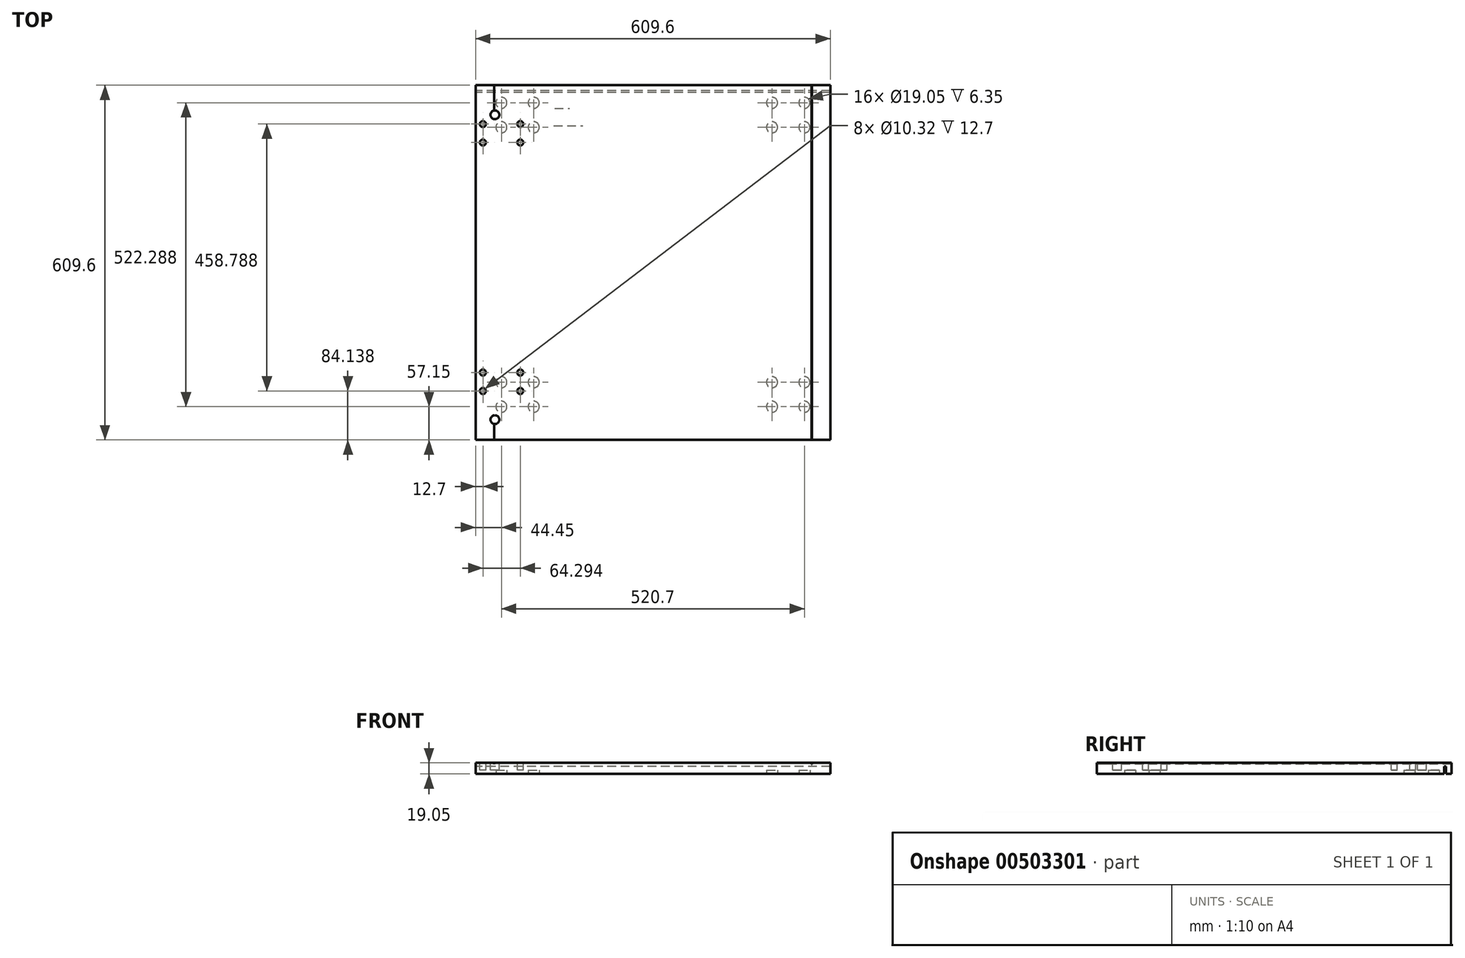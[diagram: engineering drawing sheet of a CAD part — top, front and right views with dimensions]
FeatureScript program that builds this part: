
annotation { "Feature Type Name" : "Feature", "Feature Type Description" : "" }
export const myFeature = defineFeature(function(context is Context, id is Id, definition is map)
    precondition{}
    {
        {
            var Q0;
            Q0=qCreatedBy(makeId("Top.planeOp"),FACE);
            var sketch = newSketch(context, id + "F0", { "sketchPlane" : qUnion([Q0])});
            skLineSegment(sketch, "E0.bottom", {"start": v(-304.8, 304.8) * mm, "end": v(304.8, 304.8) * mm});
            skLineSegment(sketch, "E0.top", {"start": v(-304.8, -304.8) * mm, "end": v(304.8, -304.8) * mm});
            skLineSegment(sketch, "E0.left", {"start": v(-304.8, 304.8) * mm, "end": v(-304.8, -304.8) * mm});
            skLineSegment(sketch, "E0.right", {"start": v(304.8, 304.8) * mm, "end": v(304.8, -304.8) * mm});
            skLineSegment(sketch, "E1", {"start": v(393.38, -304.8) * mm, "end": v(393.38, -188.91) * mm, "construction": true});
            skLineSegment(sketch, "E2", {"start": v(393.38, -188.91) * mm, "end": v(-304.8, -188.91) * mm, "construction": true});
            skLineSegment(sketch, "E3", {"start": v(344.85, -304.8) * mm, "end": v(344.85, -220.66) * mm, "construction": true});
            skLineSegment(sketch, "E4", {"start": v(344.85, -220.66) * mm, "end": v(-304.8, -220.66) * mm, "construction": true});
            skLineSegment(sketch, "E5", {"start": v(321.2, -304.8) * mm, "end": v(321.2, -269.88) * mm, "construction": true});
            skLineSegment(sketch, "E6", {"start": v(321.2, -269.88) * mm, "end": v(-304.8, -269.88) * mm, "construction": true});
            skLineSegment(sketch, "E7", {"start": v(-304.8, 419.45) * mm, "end": v(-227.8, 419.45) * mm, "construction": true});
            skLineSegment(sketch, "E8", {"start": v(-227.8, 419.45) * mm, "end": v(-227.8, -220.66) * mm, "construction": true});
            skPoint(sketch, "E9", {"position": v(-227.8, -188.91) * mm});
            skLineSegment(sketch, "E10", {"start": v(-304.8, 379.03) * mm, "end": v(-292.1, 379.03) * mm, "construction": true});
            skLineSegment(sketch, "E11", {"start": v(-292.1, 379.03) * mm, "end": v(-292.1, -220.66) * mm, "construction": true});
            skPoint(sketch, "E12", {"position": v(-292.1, -188.91) * mm});
            skLineSegment(sketch, "E13", {"start": v(-304.8, 399.62) * mm, "end": v(-271.46, 399.62) * mm, "construction": true});
            skLineSegment(sketch, "E14", {"start": v(-271.46, 399.62) * mm, "end": v(-271.46, -269.88) * mm, "construction": true});
            skCircle(sketch, "E15", {"center": v(-271.46, -269.88) * mm, "radius": 7.54 * mm});
            skCircle(sketch, "E16", {"center": v(-227.8, -220.66) * mm, "radius": 5.16 * mm});
            skCircle(sketch, "E17", {"center": v(-227.8, -188.91) * mm, "radius": 5.16 * mm});
            skCircle(sketch, "E18", {"center": v(-292.1, -188.91) * mm, "radius": 5.16 * mm});
            skCircle(sketch, "E19", {"center": v(-292.1, -220.66) * mm, "radius": 5.16 * mm});
            skLineSegment(sketch, "E20", {"start": v(396.02, 304.8) * mm, "end": v(396.02, 206.37) * mm, "construction": true});
            skLineSegment(sketch, "E21", {"start": v(319.7, 304.8) * mm, "end": v(319.7, 254) * mm, "construction": true});
            skLineSegment(sketch, "E22", {"start": v(353.84, 304.8) * mm, "end": v(353.84, 238.12) * mm, "construction": true});
            skLineSegment(sketch, "E23", {"start": v(319.7, 254) * mm, "end": v(-304.8, 254) * mm, "construction": true});
            skLineSegment(sketch, "E24", {"start": v(353.84, 238.12) * mm, "end": v(-304.8, 238.12) * mm, "construction": true});
            skLineSegment(sketch, "E25", {"start": v(396.02, 206.37) * mm, "end": v(-304.8, 206.38) * mm, "construction": true});
            skPoint(sketch, "E26", {"position": v(-271.46, 254) * mm});
            skPoint(sketch, "E27", {"position": v(-292.1, 238.12) * mm});
            skPoint(sketch, "E28", {"position": v(-292.1, 206.38) * mm});
            skPoint(sketch, "E29", {"position": v(-227.8, 206.38) * mm});
            skPoint(sketch, "E30", {"position": v(-227.8, 238.12) * mm});
            skCircle(sketch, "E31", {"center": v(-271.46, 254) * mm, "radius": 7.54 * mm});
            skCircle(sketch, "E32", {"center": v(-227.8, 238.12) * mm, "radius": 5.16 * mm});
            skCircle(sketch, "E33", {"center": v(-292.1, 238.12) * mm, "radius": 5.16 * mm});
            skCircle(sketch, "E34", {"center": v(-292.1, 206.38) * mm, "radius": 5.16 * mm});
            skCircle(sketch, "E35", {"center": v(-227.8, 206.38) * mm, "radius": 5.16 * mm});
            skPoint(sketch, "E36", {"position": v(0, 304.8) * mm});
            skPoint(sketch, "E37", {"position": v(304.8, 0) * mm});
            skSolve(sketch);
        }
        {
            var Q0;
            Q0=makeQuery(id+"F0.imprint","IMPRINT",FACE,{"disambiguationData":[TD([[makeQuery(id+"F0.imprint","IMPRINT",EDGE,{"derivedFrom":sQuery(id+"F0.wireOp",EDGE,"E0.bottom")}),-1.0]])]});
            var Q1;
            Q1=makeQuery(id+"F0.imprint","IMPRINT",FACE,{"disambiguationData":[TD([[makeQuery(id+"F0.imprint","IMPRINT",EDGE,{"derivedFrom":sQuery(id+"F0.wireOp",EDGE,"E31")}),1.0]])]});
            var Q2;
            Q2=makeQuery(id+"F0.imprint","IMPRINT",FACE,{"disambiguationData":[TD([[makeQuery(id+"F0.imprint","IMPRINT",EDGE,{"derivedFrom":sQuery(id+"F0.wireOp",EDGE,"E33")}),1.0]])]});
            var Q3;
            Q3=makeQuery(id+"F0.imprint","IMPRINT",FACE,{"disambiguationData":[TD([[makeQuery(id+"F0.imprint","IMPRINT",EDGE,{"derivedFrom":sQuery(id+"F0.wireOp",EDGE,"E34")}),1.0]])]});
            var Q4;
            Q4=makeQuery(id+"F0.imprint","IMPRINT",FACE,{"disambiguationData":[TD([[makeQuery(id+"F0.imprint","IMPRINT",EDGE,{"derivedFrom":sQuery(id+"F0.wireOp",EDGE,"E35")}),1.0]])]});
            var Q5;
            Q5=makeQuery(id+"F0.imprint","IMPRINT",FACE,{"disambiguationData":[TD([[makeQuery(id+"F0.imprint","IMPRINT",EDGE,{"derivedFrom":sQuery(id+"F0.wireOp",EDGE,"E32")}),1.0]])]});
            var Q6;
            Q6=makeQuery(id+"F0.imprint","IMPRINT",FACE,{"disambiguationData":[TD([[makeQuery(id+"F0.imprint","IMPRINT",EDGE,{"derivedFrom":sQuery(id+"F0.wireOp",EDGE,"E17")}),1.0]])]});
            var Q7;
            Q7=makeQuery(id+"F0.imprint","IMPRINT",FACE,{"disambiguationData":[TD([[makeQuery(id+"F0.imprint","IMPRINT",EDGE,{"derivedFrom":sQuery(id+"F0.wireOp",EDGE,"E16")}),1.0]])]});
            var Q8;
            Q8=makeQuery(id+"F0.imprint","IMPRINT",FACE,{"disambiguationData":[TD([[makeQuery(id+"F0.imprint","IMPRINT",EDGE,{"derivedFrom":sQuery(id+"F0.wireOp",EDGE,"E19")}),1.0]])]});
            var Q9;
            Q9=makeQuery(id+"F0.imprint","IMPRINT",FACE,{"disambiguationData":[TD([[makeQuery(id+"F0.imprint","IMPRINT",EDGE,{"derivedFrom":sQuery(id+"F0.wireOp",EDGE,"E18")}),1.0]])]});
            var Q10;
            Q10=makeQuery(id+"F0.imprint","IMPRINT",FACE,{"disambiguationData":[TD([[makeQuery(id+"F0.imprint","IMPRINT",EDGE,{"derivedFrom":sQuery(id+"F0.wireOp",EDGE,"E15")}),1.0]])]});
            extrude(context, id + "F1", {"entities" : qUnion([Q0, Q1, Q2, Q3, Q4, Q5, Q6, Q7, Q8, Q9, Q10]), "oppositeDirection" : true, "depth" : 19.05 * mm});
        }
        {
            var Q0;
            Q0=makeQuery(id+"F0.imprint","IMPRINT",FACE,{"disambiguationData":[TD([[makeQuery(id+"F0.imprint","IMPRINT",EDGE,{"derivedFrom":sQuery(id+"F0.wireOp",EDGE,"E15")}),1.0]])]});
            var Q1;
            Q1=makeQuery(id+"F0.imprint","IMPRINT",FACE,{"disambiguationData":[TD([[makeQuery(id+"F0.imprint","IMPRINT",EDGE,{"derivedFrom":sQuery(id+"F0.wireOp",EDGE,"E19")}),1.0]])]});
            var Q2;
            Q2=makeQuery(id+"F0.imprint","IMPRINT",FACE,{"disambiguationData":[TD([[makeQuery(id+"F0.imprint","IMPRINT",EDGE,{"derivedFrom":sQuery(id+"F0.wireOp",EDGE,"E16")}),1.0]])]});
            var Q3;
            Q3=makeQuery(id+"F0.imprint","IMPRINT",FACE,{"disambiguationData":[TD([[makeQuery(id+"F0.imprint","IMPRINT",EDGE,{"derivedFrom":sQuery(id+"F0.wireOp",EDGE,"E17")}),1.0]])]});
            var Q4;
            Q4=makeQuery(id+"F0.imprint","IMPRINT",FACE,{"disambiguationData":[TD([[makeQuery(id+"F0.imprint","IMPRINT",EDGE,{"derivedFrom":sQuery(id+"F0.wireOp",EDGE,"E18")}),1.0]])]});
            var Q5;
            Q5=makeQuery(id+"F0.imprint","IMPRINT",FACE,{"disambiguationData":[TD([[makeQuery(id+"F0.imprint","IMPRINT",EDGE,{"derivedFrom":sQuery(id+"F0.wireOp",EDGE,"E34")}),1.0]])]});
            var Q6;
            Q6=makeQuery(id+"F0.imprint","IMPRINT",FACE,{"disambiguationData":[TD([[makeQuery(id+"F0.imprint","IMPRINT",EDGE,{"derivedFrom":sQuery(id+"F0.wireOp",EDGE,"E35")}),1.0]])]});
            var Q7;
            Q7=makeQuery(id+"F0.imprint","IMPRINT",FACE,{"disambiguationData":[TD([[makeQuery(id+"F0.imprint","IMPRINT",EDGE,{"derivedFrom":sQuery(id+"F0.wireOp",EDGE,"E32")}),1.0]])]});
            var Q8;
            Q8=makeQuery(id+"F0.imprint","IMPRINT",FACE,{"disambiguationData":[TD([[makeQuery(id+"F0.imprint","IMPRINT",EDGE,{"derivedFrom":sQuery(id+"F0.wireOp",EDGE,"E33")}),1.0]])]});
            var Q9;
            Q9=makeQuery(id+"F0.imprint","IMPRINT",FACE,{"disambiguationData":[TD([[makeQuery(id+"F0.imprint","IMPRINT",EDGE,{"derivedFrom":sQuery(id+"F0.wireOp",EDGE,"E31")}),1.0]])]});
            extrude(context, id + "F2", {"entities" : qUnion([Q0, Q1, Q2, Q3, Q4, Q5, Q6, Q7, Q8, Q9]), "operationType" : NewBodyOperationType.REMOVE, "oppositeDirection" : true, "depth" : 12.7 * mm});
        }
        {
            var Q0;
            Q0=makeQuery(id+"F1.opExtrude","CAP_FACE",FACE,{"disambiguationData":[OSD([sQuery(id+"F0.wireOp",EDGE,"E0.bottom"),sQuery(id+"F0.wireOp",EDGE,"E0.top"),sQuery(id+"F0.wireOp",EDGE,"E0.left"),sQuery(id+"F0.wireOp",EDGE,"E0.right")])],"isStart":false});
            var sketch = newSketch(context, id + "F3", { "sketchPlane" : qUnion([Q0])});
            skLineSegment(sketch, "E38", {"start": v(176.5, -304.8) * mm, "end": v(176.5, -295.28) * mm, "construction": true});
            skLineSegment(sketch, "E39.bottom", {"start": v(304.8, -295.28) * mm, "end": v(-304.8, -295.28) * mm});
            skLineSegment(sketch, "E39.top", {"start": v(304.8, -292.1) * mm, "end": v(-304.8, -292.1) * mm});
            skLineSegment(sketch, "E39.left", {"start": v(304.8, -295.28) * mm, "end": v(304.8, -292.1) * mm});
            skLineSegment(sketch, "E39.right", {"start": v(-304.8, -295.28) * mm, "end": v(-304.8, -292.1) * mm});
            skSolve(sketch);
        }
        {
            var Q0;
            Q0=makeQuery(id+"F3.imprint","IMPRINT",FACE,{"disambiguationData":[TD([[makeQuery(id+"F3.imprint","IMPRINT",EDGE,{"derivedFrom":sQuery(id+"F3.wireOp",EDGE,"E39.bottom")}),-1.0]])]});
            extrude(context, id + "F4", {"entities" : qUnion([Q0]), "operationType" : NewBodyOperationType.REMOVE, "oppositeDirection" : true, "depth" : 12.7 * mm});
        }
        {
            var Q0;
            {var subQ0=sQuery(id+"F0.wireOp",EDGE,"E0.top");var subQ1=sQuery(id+"F0.wireOp",EDGE,"E0.left");var subQ2=sQuery(id+"F0.wireOp",EDGE,"E0.right");Q0=makeQuery(id+"F4.boolean.opBoolean","SPLIT",FACE,{"disambiguationData":[TD([makeQuery(id+"F1.opExtrude","SWEPT_FACE",FACE,{"disambiguationData":[OSD([subQ0])]})])],"derivedFrom":makeQuery(id+"F1.opExtrude","CAP_FACE",FACE,{"disambiguationData":[OSD([sQuery(id+"F0.wireOp",EDGE,"E0.bottom"),subQ0,subQ1,subQ2])],"isStart":false})});}
            var sketch = newSketch(context, id + "F5", { "sketchPlane" : qUnion([Q0])});
            skLineSegment(sketch, "E40", {"start": v(304.8, -324.97) * mm, "end": v(260.35, -324.97) * mm, "construction": true});
            skLineSegment(sketch, "E41", {"start": v(260.35, 304.8) * mm, "end": v(260.35, -324.35) * mm, "construction": true});
            skLineSegment(sketch, "E42", {"start": v(-304.8, -347.9) * mm, "end": v(-260.35, -347.9) * mm, "construction": true});
            skLineSegment(sketch, "E43", {"start": v(-260.35, 304.8) * mm, "end": v(-260.35, -347.28) * mm, "construction": true});
            skLineSegment(sketch, "E44", {"start": v(260.35, -324.35) * mm, "end": v(204.79, -324.35) * mm, "construction": true});
            skLineSegment(sketch, "E45", {"start": v(204.79, -324.35) * mm, "end": v(204.79, 304.8) * mm, "construction": true});
            skLineSegment(sketch, "E46", {"start": v(-260.35, -347.9) * mm, "end": v(-204.79, -347.9) * mm, "construction": true});
            skLineSegment(sketch, "E47", {"start": v(-204.79, -347.9) * mm, "end": v(-204.79, 304.8) * mm, "construction": true});
            skLineSegment(sketch, "E48", {"start": v(0, 304.8) * mm, "end": v(0, 247.65) * mm, "construction": true});
            skPoint(sketch, "E48.endSnap0", {"position": v(0, 304.8) * mm});
            skLineSegment(sketch, "E49", {"start": v(260.35, 247.65) * mm, "end": v(-260.35, 247.65) * mm, "construction": true});
            skLineSegment(sketch, "E50.0", {"start": v(-304.8, -304.8) * mm, "end": v(304.8, -304.8) * mm});
            skLineSegment(sketch, "E51", {"start": v(0, -304.8) * mm, "end": v(0, -274.64) * mm, "construction": true});
            skPoint(sketch, "E51.endSnap0", {"position": v(0, -292.1) * mm});
            skLineSegment(sketch, "E52", {"start": v(260.35, -274.64) * mm, "end": v(-260.35, -274.64) * mm, "construction": true});
            skLineSegment(sketch, "E53", {"start": v(0, 247.65) * mm, "end": v(0, 205.58) * mm, "construction": true});
            skLineSegment(sketch, "E54", {"start": v(0, -274.64) * mm, "end": v(0, -232.57) * mm, "construction": true});
            skLineSegment(sketch, "E55", {"start": v(260.35, -232.57) * mm, "end": v(-260.35, -232.57) * mm, "construction": true});
            skLineSegment(sketch, "E56", {"start": v(260.35, 205.58) * mm, "end": v(-260.35, 205.58) * mm, "construction": true});
            skCircle(sketch, "E57", {"center": v(260.35, 205.58) * mm, "radius": 9.53 * mm});
            skCircle(sketch, "E58", {"center": v(204.79, 205.58) * mm, "radius": 9.53 * mm});
            skCircle(sketch, "E59", {"center": v(204.79, 247.65) * mm, "radius": 9.53 * mm});
            skCircle(sketch, "E60", {"center": v(-204.79, 205.58) * mm, "radius": 9.53 * mm});
            skCircle(sketch, "E61", {"center": v(260.35, 247.65) * mm, "radius": 9.53 * mm});
            skCircle(sketch, "E62", {"center": v(-260.35, 205.58) * mm, "radius": 9.53 * mm});
            skCircle(sketch, "E63", {"center": v(260.35, -232.57) * mm, "radius": 9.53 * mm});
            skCircle(sketch, "E64", {"center": v(204.79, -232.57) * mm, "radius": 9.53 * mm});
            skCircle(sketch, "E65", {"center": v(204.79, -274.64) * mm, "radius": 9.53 * mm});
            skCircle(sketch, "E66", {"center": v(260.35, -274.64) * mm, "radius": 9.53 * mm});
            skCircle(sketch, "E67", {"center": v(-204.79, -274.64) * mm, "radius": 9.53 * mm});
            skCircle(sketch, "E68", {"center": v(-260.35, -274.64) * mm, "radius": 9.53 * mm});
            skCircle(sketch, "E69", {"center": v(-260.35, -232.57) * mm, "radius": 9.53 * mm});
            skCircle(sketch, "E70", {"center": v(-204.79, -232.57) * mm, "radius": 9.53 * mm});
            skCircle(sketch, "E71", {"center": v(-260.35, 247.65) * mm, "radius": 9.53 * mm});
            skCircle(sketch, "E72", {"center": v(-204.79, 247.65) * mm, "radius": 9.53 * mm});
            skSolve(sketch);
        }
        {
            var Q0;
            Q0=makeQuery(id+"F5.imprint","IMPRINT",FACE,{"disambiguationData":[TD([[makeQuery(id+"F5.imprint","IMPRINT",EDGE,{"derivedFrom":sQuery(id+"F5.wireOp",EDGE,"E66")}),1.0]])]});
            var Q1;
            Q1=makeQuery(id+"F5.imprint","IMPRINT",FACE,{"disambiguationData":[TD([[makeQuery(id+"F5.imprint","IMPRINT",EDGE,{"derivedFrom":sQuery(id+"F5.wireOp",EDGE,"E65")}),1.0]])]});
            var Q2;
            Q2=makeQuery(id+"F5.imprint","IMPRINT",FACE,{"disambiguationData":[TD([[makeQuery(id+"F5.imprint","IMPRINT",EDGE,{"derivedFrom":sQuery(id+"F5.wireOp",EDGE,"E64")}),1.0]])]});
            var Q3;
            Q3=makeQuery(id+"F5.imprint","IMPRINT",FACE,{"disambiguationData":[TD([[makeQuery(id+"F5.imprint","IMPRINT",EDGE,{"derivedFrom":sQuery(id+"F5.wireOp",EDGE,"E63")}),1.0]])]});
            var Q4;
            Q4=makeQuery(id+"F5.imprint","IMPRINT",FACE,{"disambiguationData":[TD([[makeQuery(id+"F5.imprint","IMPRINT",EDGE,{"derivedFrom":sQuery(id+"F5.wireOp",EDGE,"E67")}),1.0]])]});
            var Q5;
            Q5=makeQuery(id+"F5.imprint","IMPRINT",FACE,{"disambiguationData":[TD([[makeQuery(id+"F5.imprint","IMPRINT",EDGE,{"derivedFrom":sQuery(id+"F5.wireOp",EDGE,"E68")}),1.0]])]});
            var Q6;
            Q6=makeQuery(id+"F5.imprint","IMPRINT",FACE,{"disambiguationData":[TD([[makeQuery(id+"F5.imprint","IMPRINT",EDGE,{"derivedFrom":sQuery(id+"F5.wireOp",EDGE,"E69")}),1.0]])]});
            var Q7;
            Q7=makeQuery(id+"F5.imprint","IMPRINT",FACE,{"disambiguationData":[TD([[makeQuery(id+"F5.imprint","IMPRINT",EDGE,{"derivedFrom":sQuery(id+"F5.wireOp",EDGE,"E70")}),1.0]])]});
            var Q8;
            Q8=makeQuery(id+"F5.imprint","IMPRINT",FACE,{"disambiguationData":[TD([[makeQuery(id+"F5.imprint","IMPRINT",EDGE,{"derivedFrom":sQuery(id+"F5.wireOp",EDGE,"E60")}),1.0]])]});
            var Q9;
            Q9=makeQuery(id+"F5.imprint","IMPRINT",FACE,{"disambiguationData":[TD([[makeQuery(id+"F5.imprint","IMPRINT",EDGE,{"derivedFrom":sQuery(id+"F5.wireOp",EDGE,"E62")}),1.0]])]});
            var Q10;
            Q10=makeQuery(id+"F5.imprint","IMPRINT",FACE,{"disambiguationData":[TD([[makeQuery(id+"F5.imprint","IMPRINT",EDGE,{"derivedFrom":sQuery(id+"F5.wireOp",EDGE,"E71")}),1.0]])]});
            var Q11;
            Q11=makeQuery(id+"F5.imprint","IMPRINT",FACE,{"disambiguationData":[TD([[makeQuery(id+"F5.imprint","IMPRINT",EDGE,{"derivedFrom":sQuery(id+"F5.wireOp",EDGE,"E72")}),1.0]])]});
            var Q12;
            Q12=makeQuery(id+"F5.imprint","IMPRINT",FACE,{"disambiguationData":[TD([[makeQuery(id+"F5.imprint","IMPRINT",EDGE,{"derivedFrom":sQuery(id+"F5.wireOp",EDGE,"E59")}),1.0]])]});
            var Q13;
            Q13=makeQuery(id+"F5.imprint","IMPRINT",FACE,{"disambiguationData":[TD([[makeQuery(id+"F5.imprint","IMPRINT",EDGE,{"derivedFrom":sQuery(id+"F5.wireOp",EDGE,"E58")}),1.0]])]});
            var Q14;
            Q14=makeQuery(id+"F5.imprint","IMPRINT",FACE,{"disambiguationData":[TD([[makeQuery(id+"F5.imprint","IMPRINT",EDGE,{"derivedFrom":sQuery(id+"F5.wireOp",EDGE,"E57")}),1.0]])]});
            var Q15;
            Q15=makeQuery(id+"F5.imprint","IMPRINT",FACE,{"disambiguationData":[TD([[makeQuery(id+"F5.imprint","IMPRINT",EDGE,{"derivedFrom":sQuery(id+"F5.wireOp",EDGE,"E61")}),1.0]])]});
            extrude(context, id + "F6", {"entities" : qUnion([Q0, Q1, Q2, Q3, Q4, Q5, Q6, Q7, Q8, Q9, Q10, Q11, Q12, Q13, Q14, Q15]), "operationType" : NewBodyOperationType.REMOVE, "oppositeDirection" : true, "depth" : 6.35 * mm});
        }
        {
            var Q0;
            {var subQ0=sQuery(id+"F0.wireOp",EDGE,"E0.top");var subQ1=sQuery(id+"F0.wireOp",EDGE,"E0.left");var subQ2=sQuery(id+"F0.wireOp",EDGE,"E0.right");Q0=makeQuery(id+"F4.boolean.opBoolean","SPLIT",FACE,{"disambiguationData":[TD([makeQuery(id+"F1.opExtrude","SWEPT_FACE",FACE,{"disambiguationData":[OSD([subQ0])]})])],"derivedFrom":makeQuery(id+"F1.opExtrude","CAP_FACE",FACE,{"disambiguationData":[OSD([sQuery(id+"F0.wireOp",EDGE,"E0.bottom"),subQ0,subQ1,subQ2])],"isStart":false})});}
            var sketch = newSketch(context, id + "F7", { "sketchPlane" : qUnion([Q0])});
            skLineSegment(sketch, "E73.bottom", {"start": v(-168.75, -265.08) * mm, "end": v(-143.35, -265.08) * mm});
            skLineSegment(sketch, "E73.top", {"start": v(-168.75, -265.06) * mm, "end": v(-143.35, -265.06) * mm});
            skLineSegment(sketch, "E73.left", {"start": v(-168.75, -265.08) * mm, "end": v(-168.75, -265.06) * mm});
            skLineSegment(sketch, "E73.right", {"start": v(-143.35, -265.08) * mm, "end": v(-143.35, -265.06) * mm});
            skLineSegment(sketch, "E74.bottom", {"start": v(-170.19, -234.87) * mm, "end": v(-120.19, -234.87) * mm});
            skLineSegment(sketch, "E74.top", {"start": v(-170.19, -234.9) * mm, "end": v(-120.19, -234.9) * mm});
            skLineSegment(sketch, "E74.left", {"start": v(-170.19, -234.87) * mm, "end": v(-170.19, -234.9) * mm});
            skLineSegment(sketch, "E74.right", {"start": v(-120.19, -234.87) * mm, "end": v(-120.19, -234.9) * mm});
            skSolve(sketch);
        }
        {
            var Q0;
            Q0=makeQuery(id+"F7.imprint","IMPRINT",FACE,{"disambiguationData":[TD([[makeQuery(id+"F7.imprint","IMPRINT",EDGE,{"derivedFrom":sQuery(id+"F7.wireOp",EDGE,"E73.bottom")}),1.0]])]});
            var Q1;
            Q1=makeQuery(id+"F7.imprint","IMPRINT",FACE,{"disambiguationData":[TD([[makeQuery(id+"F7.imprint","IMPRINT",EDGE,{"derivedFrom":sQuery(id+"F7.wireOp",EDGE,"E74.bottom")}),-1.0]])]});
            extrude(context, id + "F8", {"entities" : qUnion([Q0, Q1]), "operationType" : NewBodyOperationType.REMOVE, "oppositeDirection" : true, "depth" : 0.25 * mm});
        }
        {
            var Q0;
            Q0=makeQuery(id+"F1.opExtrude","CAP_FACE",FACE,{"disambiguationData":[OSD([sQuery(id+"F0.wireOp",EDGE,"E0.bottom"),sQuery(id+"F0.wireOp",EDGE,"E0.top"),sQuery(id+"F0.wireOp",EDGE,"E0.left"),sQuery(id+"F0.wireOp",EDGE,"E0.right")])],"isStart":true});
            var sketch = newSketch(context, id + "F9", { "sketchPlane" : qUnion([Q0])});
            skLineSegment(sketch, "E75", {"start": v(-304.8, 8.16) * mm, "end": v(-273.05, 8.16) * mm, "construction": true});
            skLineSegment(sketch, "E76.bottom", {"start": v(-273.05, 304.8) * mm, "end": v(-273.02, 304.8) * mm});
            skLineSegment(sketch, "E76.top", {"start": v(-273.05, -304.8) * mm, "end": v(-273.02, -304.8) * mm});
            skLineSegment(sketch, "E76.left", {"start": v(-273.05, 304.8) * mm, "end": v(-273.05, -304.8) * mm});
            skLineSegment(sketch, "E76.right", {"start": v(-273.02, 304.8) * mm, "end": v(-273.02, -304.8) * mm});
            skLineSegment(sketch, "E77.MirrorCS", {"start": v(273.05, 304.8) * mm, "end": v(273.05, -304.8) * mm});
            skLineSegment(sketch, "E78.MirrorCS", {"start": v(273.05, -304.8) * mm, "end": v(273.02, -304.8) * mm});
            skLineSegment(sketch, "E79.MirrorCS", {"start": v(273.02, 304.8) * mm, "end": v(273.02, -304.8) * mm});
            skLineSegment(sketch, "E80.MirrorCS", {"start": v(273.05, 304.8) * mm, "end": v(273.02, 304.8) * mm});
            skSolve(sketch);
        }
        {
            var Q0;
            {var subQ0=sQuery(id+"F9.wireOp",EDGE,"E76.left");var subQ1=makeQuery(id+"F2.boolean.opBoolean","COPY",EDGE,{"derivedFrom":makeQuery(id+"F2.opExtrude","CAP_EDGE",EDGE,{"disambiguationData":[OSD([sQuery(id+"F0.wireOp",EDGE,"E31")])],"isStart":true})});var subQ2=makeQuery(id+"F9.imprint","INTERSECT",VERTEX,{"disambiguationData":[OD(1.0)],"derivedFrom":[subQ1,subQ0]});Q0=makeQuery(id+"F9.imprint","IMPRINT",FACE,{"disambiguationData":[TD([[makeQuery(id+"F9.imprint","IMPRINT",EDGE,{"disambiguationData":[TD([[subQ2,-1.0]])],"derivedFrom":subQ0}),1.0]])]});}
            var Q1;
            {var subQ0=sQuery(id+"F9.wireOp",EDGE,"E76.left");var subQ1=makeQuery(id+"F2.boolean.opBoolean","COPY",EDGE,{"derivedFrom":makeQuery(id+"F2.opExtrude","CAP_EDGE",EDGE,{"disambiguationData":[OSD([sQuery(id+"F0.wireOp",EDGE,"E31")])],"isStart":true})});var subQ2=makeQuery(id+"F9.imprint","INTERSECT",VERTEX,{"disambiguationData":[OD(0.0)],"derivedFrom":[subQ1,subQ0]});Q1=makeQuery(id+"F9.imprint","IMPRINT",FACE,{"disambiguationData":[TD([[makeQuery(id+"F9.imprint","IMPRINT",EDGE,{"disambiguationData":[TD([[subQ2,-1.0]])],"derivedFrom":subQ0}),1.0]])]});}
            var Q2;
            {var subQ0=sQuery(id+"F9.wireOp",EDGE,"E76.bottom");Q2=makeQuery(id+"F9.imprint","IMPRINT",FACE,{"disambiguationData":[TD([[makeQuery(id+"F9.imprint","IMPRINT",EDGE,{"derivedFrom":subQ0}),-1.0]])]});}
            var Q3;
            {var subQ0=sQuery(id+"F9.wireOp",EDGE,"E76.left");var subQ1=makeQuery(id+"F2.boolean.opBoolean","COPY",EDGE,{"derivedFrom":makeQuery(id+"F2.opExtrude","CAP_EDGE",EDGE,{"disambiguationData":[OSD([sQuery(id+"F0.wireOp",EDGE,"E15")])],"isStart":true})});var subQ2=makeQuery(id+"F9.imprint","INTERSECT",VERTEX,{"disambiguationData":[OD(0.0)],"derivedFrom":[subQ1,subQ0]});Q3=makeQuery(id+"F9.imprint","IMPRINT",FACE,{"disambiguationData":[TD([[makeQuery(id+"F9.imprint","IMPRINT",EDGE,{"disambiguationData":[TD([[subQ2,-1.0]])],"derivedFrom":subQ0}),1.0]])]});}
            var Q4;
            {var subQ0=sQuery(id+"F9.wireOp",EDGE,"E76.top");Q4=makeQuery(id+"F9.imprint","IMPRINT",FACE,{"disambiguationData":[TD([[makeQuery(id+"F9.imprint","IMPRINT",EDGE,{"derivedFrom":subQ0}),1.0]])]});}
            var Q5;
            {var subQ0=sQuery(id+"F9.wireOp",EDGE,"E78.MirrorCS");Q5=makeQuery(id+"F9.imprint","IMPRINT",FACE,{"disambiguationData":[TD([[makeQuery(id+"F9.imprint","IMPRINT",EDGE,{"derivedFrom":subQ0}),1.0]])]});}
            var Q6;
            {var subQ0=sQuery(id+"F9.wireOp",EDGE,"E77.MirrorCS");var subQ1=makeQuery(id+"FkhFIqLiuisktci_1.1.F2.boolean.opBoolean","COPY",EDGE,{"derivedFrom":makeQuery(id+"FkhFIqLiuisktci_1.1.F2.opExtrude","CAP_EDGE",EDGE,{"disambiguationData":[OSD([sQuery(id+"F0.wireOp",EDGE,"E15")])],"isStart":true})});var subQ2=makeQuery(id+"F9.imprint","INTERSECT",VERTEX,{"disambiguationData":[OD(0.0)],"derivedFrom":[subQ1,subQ0]});Q6=makeQuery(id+"F9.imprint","IMPRINT",FACE,{"disambiguationData":[TD([[makeQuery(id+"F9.imprint","IMPRINT",EDGE,{"disambiguationData":[TD([[subQ2,-1.0]])],"derivedFrom":subQ0}),-1.0]])]});}
            var Q7;
            {var subQ0=sQuery(id+"F9.wireOp",EDGE,"E77.MirrorCS");var subQ1=makeQuery(id+"FkhFIqLiuisktci_1.1.F2.boolean.opBoolean","COPY",EDGE,{"derivedFrom":makeQuery(id+"FkhFIqLiuisktci_1.1.F2.opExtrude","CAP_EDGE",EDGE,{"disambiguationData":[OSD([sQuery(id+"F0.wireOp",EDGE,"E31")])],"isStart":true})});var subQ2=makeQuery(id+"F9.imprint","INTERSECT",VERTEX,{"disambiguationData":[OD(1.0)],"derivedFrom":[subQ1,subQ0]});Q7=makeQuery(id+"F9.imprint","IMPRINT",FACE,{"disambiguationData":[TD([[makeQuery(id+"F9.imprint","IMPRINT",EDGE,{"disambiguationData":[TD([[subQ2,-1.0]])],"derivedFrom":subQ0}),-1.0]])]});}
            var Q8;
            {var subQ0=sQuery(id+"F9.wireOp",EDGE,"E77.MirrorCS");var subQ1=makeQuery(id+"FkhFIqLiuisktci_1.1.F2.boolean.opBoolean","COPY",EDGE,{"derivedFrom":makeQuery(id+"FkhFIqLiuisktci_1.1.F2.opExtrude","CAP_EDGE",EDGE,{"disambiguationData":[OSD([sQuery(id+"F0.wireOp",EDGE,"E31")])],"isStart":true})});var subQ2=makeQuery(id+"F9.imprint","INTERSECT",VERTEX,{"disambiguationData":[OD(0.0)],"derivedFrom":[subQ1,subQ0]});Q8=makeQuery(id+"F9.imprint","IMPRINT",FACE,{"disambiguationData":[TD([[makeQuery(id+"F9.imprint","IMPRINT",EDGE,{"disambiguationData":[TD([[subQ2,-1.0]])],"derivedFrom":subQ0}),-1.0]])]});}
            var Q9;
            {var subQ0=sQuery(id+"F9.wireOp",EDGE,"E80.MirrorCS");Q9=makeQuery(id+"F9.imprint","IMPRINT",FACE,{"disambiguationData":[TD([[makeQuery(id+"F9.imprint","IMPRINT",EDGE,{"derivedFrom":subQ0}),-1.0]])]});}
            extrude(context, id + "F10", {"entities" : qUnion([Q0, Q1, Q2, Q3, Q4, Q5, Q6, Q7, Q8, Q9]), "operationType" : NewBodyOperationType.REMOVE, "oppositeDirection" : true, "depth" : 2.54 * mm});
        }
    });
